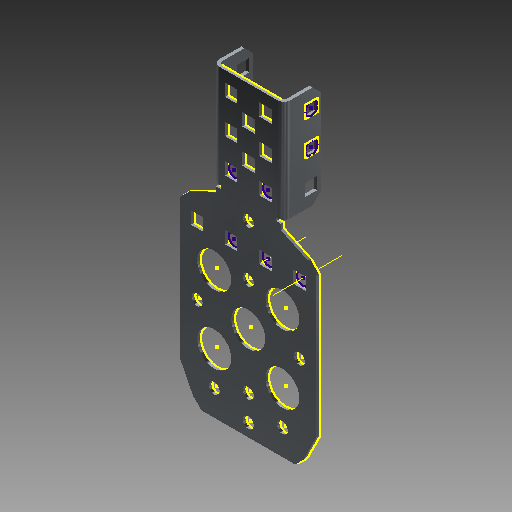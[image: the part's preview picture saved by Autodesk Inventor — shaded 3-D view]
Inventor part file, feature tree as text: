
AUTODESK INVENTOR PART (.ipt)
format: ipt  version: 2018 (Build 220112000, 112)  size: 540,672 bytes
history: native  units: in
note: dims shown in document units (in); Inventor stores cm internally (conversion verified against a paired STEP export)
features: other x14, sketch x8, sheet_metal_op x5, extrude x5
ambient origin geometry x8: Origin, YZ Plane, XZ Plane, XY Plane, X Axis, Y Axis, Z Axis, Center Point
bodies: Solid1 (feature_tree)
feature tree (32):
  sheet_metal_op  "Face1"
  sheet_metal_op  "Face2"
  sheet_metal_op  "Face3"
  other  "Corner Chamfer1"
  sketch  "Sketch7"  dims[d22=1.5in]
  sketch  "Sketch8"  dims[d23=0.046in]
  other  "Work Axis1"
  other  "Work Axis2"
  sketch  "Sketch9"  dims[d24=0.046in d25=0.023in d26=0.092in d27=0.046in d28=0.5in d29=1.5in d30=0.046in d31=0.046in d32=0.023in d33=0.092in d34=0.046in d35=0.046in d36=0.0in d37=0.125in d38=0.25in d39=45.0deg d40=0.046in d41=0.0in d42=1.0in d43=0.0in d44=1.0in d45=0.0in d46=1.0in d47=0.0in d48=1.0in d49=0.0in d50=1.0in d51=0.0in d52=0.046in]
  sketch  "Sketch1"  dims[d1=1.1811in d3=0.7874in d5=1.5748in d7=0.3937in d8=0.5in d9=0.5in d10=0.5in d11=1.0in d12=0.25in d13=0.951in]
  other  "Plate1"
  sketch  "Sketch2"  dims[d14=1.625in d15=4.5in]
  other  "Plate2"
  sheet_metal_op  "Bend1"
  sketch  "Sketch3"  dims[d16=2.0in d17=0.163in]
  other  "Plate3"
  sheet_metal_op  "Bend2"
  sketch  "Sketch4"  dims[d18=0.182in d19=0.182in]
  sketch  "Sketch5"  dims[d20=0.046in d21=0.5in]
  other  "Srf1"
  other  "Srf2"
  other  "Srf3"
  other  "Srf4"
  other  "Srf5"
  other  "Cut1"
  other  "Cut2"
  extrude  "ExtrusionSrf1"  Depth=0.951in
  extrude  "ExtrusionSrf2"  Depth=4.5in
  extrude  "ExtrusionSrf3"  Depth=2.0in
  extrude  "ExtrusionSrf4"  Depth=0.182in
  extrude  "ExtrusionSrf5"  Depth=0.5in
  other  "Definition1"
